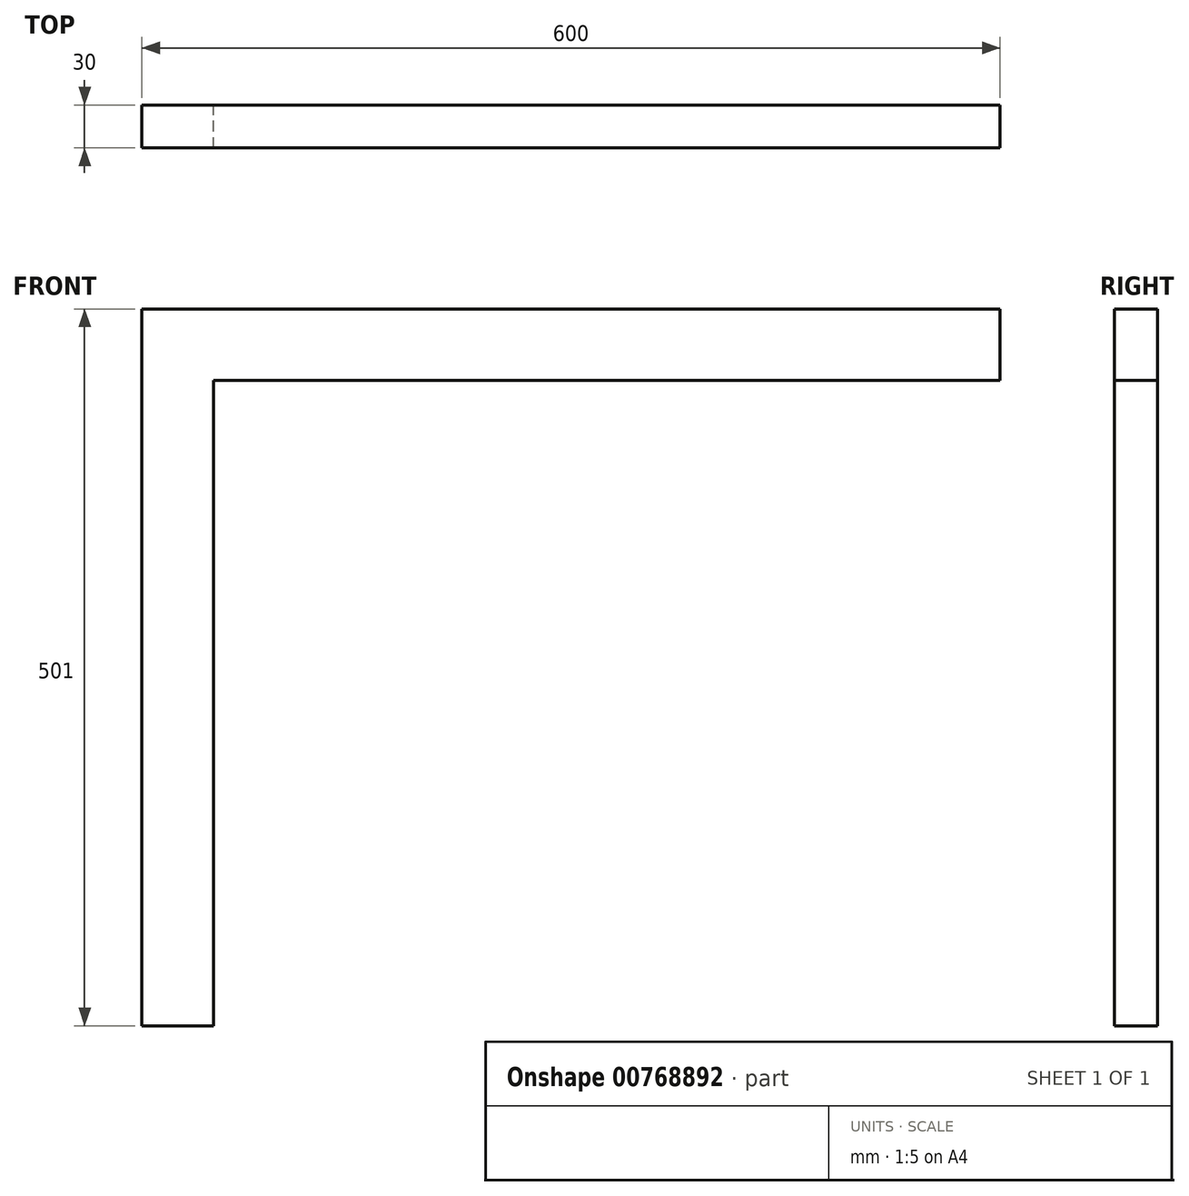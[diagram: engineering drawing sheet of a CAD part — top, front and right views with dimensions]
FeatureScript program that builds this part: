
annotation { "Feature Type Name" : "Feature", "Feature Type Description" : "" }
export const myFeature = defineFeature(function(context is Context, id is Id, definition is map)
    precondition{}
    {
        {
            var Q0;
            Q0=qCreatedBy(makeId("Front.planeOp"),FACE);
            var sketch = newSketch(context, id + "F0", { "sketchPlane" : qUnion([Q0])});
            skLineSegment(sketch, "E0.bottom", {"start": v(0, 0) * mm, "end": v(50, 0) * mm});
            skLineSegment(sketch, "E0.top", {"start": v(0, -501) * mm, "end": v(50, -501) * mm});
            skLineSegment(sketch, "E0.left", {"start": v(0, 0) * mm, "end": v(0, -501) * mm});
            skLineSegment(sketch, "E0.right", {"start": v(50, 0) * mm, "end": v(50, -501) * mm});
            skLineSegment(sketch, "E1.bottom", {"start": v(0, 0) * mm, "end": v(600, 0) * mm});
            skLineSegment(sketch, "E1.top", {"start": v(0, -50) * mm, "end": v(600, -50) * mm});
            skLineSegment(sketch, "E1.left", {"start": v(0, 0) * mm, "end": v(0, -50) * mm});
            skLineSegment(sketch, "E1.right", {"start": v(600, 0) * mm, "end": v(600, -50) * mm});
            skSolve(sketch);
        }
        {
            var Q0;
            Q0 = qSketchRegion(id + "F0", true);
            extrude(context, id + "F1", {"entities" : qUnion([Q0]), "depth" : 30 * mm, "offsetDistance" : 25 * mm});
        }
    });
